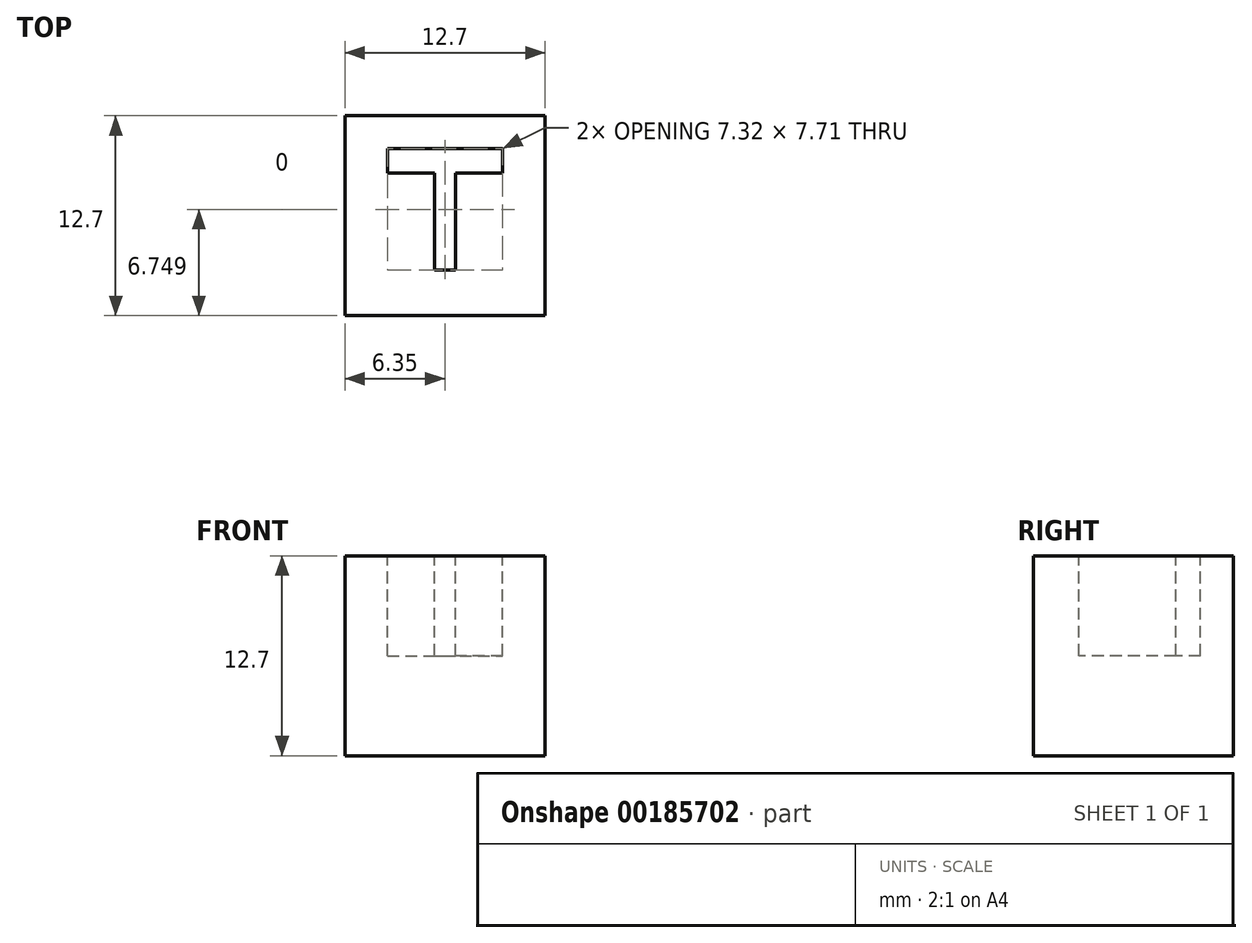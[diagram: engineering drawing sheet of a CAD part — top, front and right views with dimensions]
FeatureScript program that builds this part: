
annotation { "Feature Type Name" : "Feature", "Feature Type Description" : "" }
export const myFeature = defineFeature(function(context is Context, id is Id, definition is map)
    precondition{}
    {
        {
            var Q0;
            Q0=qCreatedBy(makeId("Top.planeOp"),FACE);
            var sketch = newSketch(context, id + "F0", { "sketchPlane" : qUnion([Q0])});
            skLineSegment(sketch, "E0.bottom", {"start": v(0, 0) * mm, "end": v(6.35, 0) * mm});
            skLineSegment(sketch, "E0.top", {"start": v(0, 12.7) * mm, "end": v(6.35, 12.7) * mm});
            skLineSegment(sketch, "E0.right", {"start": v(6.35, 0) * mm, "end": v(6.35, 12.7) * mm});
            skLineSegment(sketch, "E1.bottom", {"start": v(0, 0) * mm, "end": v(-6.35, 0) * mm});
            skLineSegment(sketch, "E1.top", {"start": v(-5.16, 12.7) * mm, "end": v(-6.35, 12.7) * mm});
            skLineSegment(sketch, "E1.right", {"start": v(-6.35, 0) * mm, "end": v(-6.35, 12.7) * mm});
            skLineSegment(sketch, "E2", {"start": v(0, 12.7) * mm, "end": v(0, 0) * mm, "construction": true});
            skLineSegment(sketch, "E3", {"start": v(0, 12.7) * mm, "end": v(-5.16, 12.7) * mm});
            skSolve(sketch);
        }
        {
            var Q0;
            Q0=makeQuery(id+"F0.imprint","IMPRINT",FACE,{"disambiguationData":[TD([[makeQuery(id+"F0.imprint","IMPRINT",EDGE,{"derivedFrom":sQuery(id+"F0.wireOp",EDGE,"E0.bottom")}),1.0]])]});
            extrude(context, id + "F1", {"entities" : qUnion([Q0]), "depth" : 12.7 * mm});
        }
        {
            var Q0;
            Q0=makeQuery(id+"F1.opExtrude","CAP_FACE",FACE,{"disambiguationData":[OSD([sQuery(id+"F0.wireOp",EDGE,"E0.bottom"),sQuery(id+"F0.wireOp",EDGE,"E0.top"),sQuery(id+"F0.wireOp",EDGE,"E0.right"),sQuery(id+"F0.wireOp",EDGE,"E1.bottom"),sQuery(id+"F0.wireOp",EDGE,"E1.top"),sQuery(id+"F0.wireOp",EDGE,"E1.right"),sQuery(id+"F0.wireOp",EDGE,"E3")])],"isStart":false});
            var sketch = newSketch(context, id + "F2", { "sketchPlane" : qUnion([Q0])});
            skLineSegment(sketch, "E4", {"start": v(0, 12.7) * mm, "end": v(0, 0) * mm, "construction": true});
            skLineSegment(sketch, "E5", {"start": v(0, 10.6) * mm, "end": v(3.66, 10.6) * mm});
            skLineSegment(sketch, "E6", {"start": v(3.66, 10.6) * mm, "end": v(3.66, 9.05) * mm});
            skLineSegment(sketch, "E7", {"start": v(3.66, 9.05) * mm, "end": v(0.68, 9.05) * mm});
            skLineSegment(sketch, "E8", {"start": v(0.68, 9.05) * mm, "end": v(0.68, 2.9) * mm});
            skLineSegment(sketch, "E9", {"start": v(0.68, 2.9) * mm, "end": v(0, 2.9) * mm});
            skLineSegment(sketch, "E10.MirrorCS", {"start": v(-0.68, 2.9) * mm, "end": v(0, 2.9) * mm});
            skLineSegment(sketch, "E11.MirrorCS", {"start": v(-0.68, 9.05) * mm, "end": v(-0.68, 2.9) * mm});
            skLineSegment(sketch, "E12.MirrorCS", {"start": v(-3.66, 10.6) * mm, "end": v(-3.66, 9.05) * mm});
            skLineSegment(sketch, "E13.MirrorCS", {"start": v(-3.66, 9.05) * mm, "end": v(-0.68, 9.05) * mm});
            skLineSegment(sketch, "E14.MirrorCS", {"start": v(0, 10.6) * mm, "end": v(-3.66, 10.6) * mm});
            skSolve(sketch);
        }
        {
            var Q0;
            Q0=makeQuery(id+"F2.imprint","IMPRINT",FACE,{"disambiguationData":[TD([[makeQuery(id+"F2.imprint","IMPRINT",EDGE,{"derivedFrom":sQuery(id+"F2.wireOp",EDGE,"E5")}),-1.0]])]});
            extrude(context, id + "F3", {"entities" : qUnion([Q0]), "operationType" : NewBodyOperationType.REMOVE, "oppositeDirection" : true, "depth" : 6.35 * mm});
        }
    });
